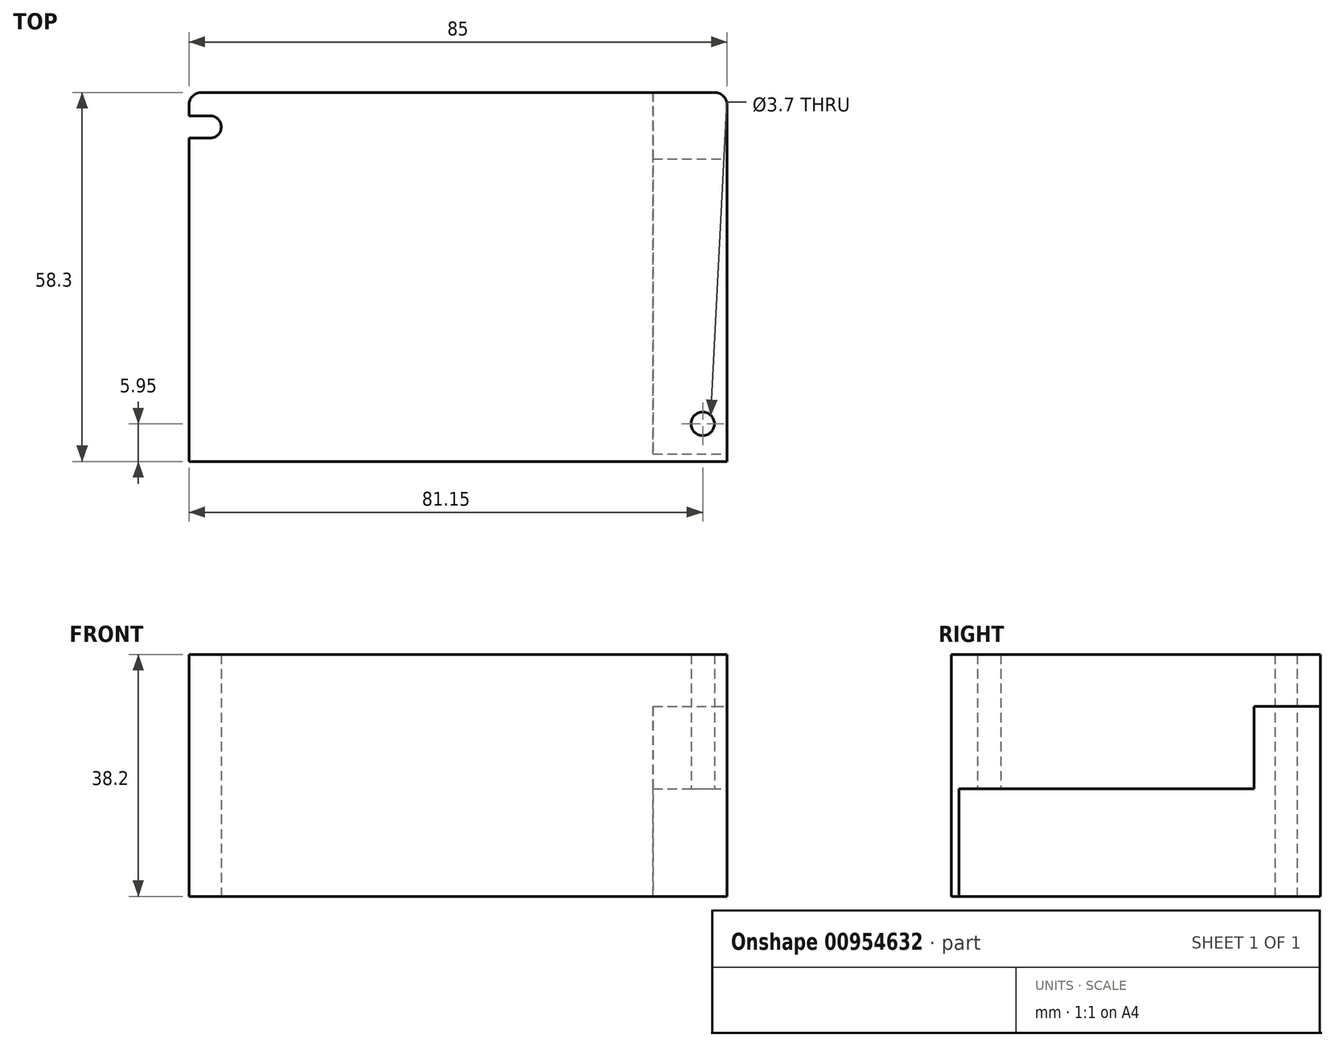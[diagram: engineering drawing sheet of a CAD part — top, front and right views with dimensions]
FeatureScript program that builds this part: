
annotation { "Feature Type Name" : "Feature", "Feature Type Description" : "" }
export const myFeature = defineFeature(function(context is Context, id is Id, definition is map)
    precondition{}
    {
        {
            var Q0;
            Q0=qCreatedBy(makeId("Top.planeOp"),FACE);
            var sketch = newSketch(context, id + "F0", { "sketchPlane" : qUnion([Q0])});
            skLineSegment(sketch, "E0.bottom", {"start": v(40.5, 29.15) * mm, "end": v(-40.5, 29.15) * mm});
            skLineSegment(sketch, "E0.top", {"start": v(42.5, -29.15) * mm, "end": v(-42.5, -29.15) * mm});
            skLineSegment(sketch, "E0.left", {"start": v(42.5, 27.15) * mm, "end": v(42.5, -29.15) * mm});
            skLineSegment(sketch, "E0.right", {"start": v(-42.5, 27.15) * mm, "end": v(-42.5, -29.15) * mm});
            skPoint(sketch, "E0.middle", {"position": v(0, 0) * mm});
            skPoint(sketch, "E1.visualSharp", {"position": v(-42.5, 29.15) * mm});
            skArc(sketch, "E1.filletArc", {"start": v(-40.5, 29.15) * mm, "mid": v(-41.91, 28.56) * mm, "end": v(-42.5, 27.15) * mm});
            skPoint(sketch, "E2.visualSharp", {"position": v(42.5, 29.15) * mm});
            skArc(sketch, "E2.filletArc", {"start": v(42.5, 27.15) * mm, "mid": v(41.91, 28.56) * mm, "end": v(40.5, 29.15) * mm});
            skLineSegment(sketch, "E3", {"start": v(-42.5, 25.45) * mm, "end": v(-39.15, 25.45) * mm});
            skLineSegment(sketch, "E4", {"start": v(-42.5, 21.95) * mm, "end": v(-39.15, 21.95) * mm});
            skArc(sketch, "E5", {"start": v(-39.15, 25.45) * mm, "mid": v(-37.4, 23.7) * mm, "end": v(-39.15, 21.95) * mm});
            skCircle(sketch, "E6", {"center": v(38.65, -23.2) * mm, "radius": 1.85 * mm});
            skSolve(sketch);
        }
        {
            var Q0;
            Q0=makeQuery(id+"F0.imprint","IMPRINT",FACE,{"disambiguationData":[TD([[makeQuery(id+"F0.imprint","IMPRINT",EDGE,{"derivedFrom":sQuery(id+"F0.wireOp",EDGE,"E0.bottom")}),1.0]])]});
            extrude(context, id + "F1", {"entities" : qUnion([Q0]), "depth" : 38.2 * mm, "offsetDistance" : 25 * mm});
        }
        {
            var Q0;
            Q0=makeQuery(id+"F1.opExtrude","SWEPT_FACE",FACE,{"disambiguationData":[OSD([sQuery(id+"F0.wireOp",EDGE,"E0.left")])]});
            var sketch = newSketch(context, id + "F2", { "sketchPlane" : qUnion([Q0])});
            skLineSegment(sketch, "E7.0.0", {"start": v(-29.15, 0) * mm, "end": v(27.15, 0) * mm});
            skLineSegment(sketch, "E7.0.1", {"start": v(27.15, 0) * mm, "end": v(27.15, 38.2) * mm});
            skLineSegment(sketch, "E7.0.2", {"start": v(27.15, 38.2) * mm, "end": v(-29.15, 38.2) * mm});
            skLineSegment(sketch, "E7.0.3", {"start": v(-29.15, 38.2) * mm, "end": v(-29.15, 0) * mm});
            skLineSegment(sketch, "E8", {"start": v(-27.95, 0) * mm, "end": v(-27.95, 17) * mm});
            skLineSegment(sketch, "E9", {"start": v(-27.95, 17) * mm, "end": v(18.65, 17) * mm});
            skLineSegment(sketch, "E10", {"start": v(18.65, 17) * mm, "end": v(18.65, 30) * mm});
            skLineSegment(sketch, "E11", {"start": v(18.65, 30) * mm, "end": v(29.15, 30) * mm});
            skLineSegment(sketch, "E12", {"start": v(29.15, 30) * mm, "end": v(29.15, 0) * mm});
            skLineSegment(sketch, "E13", {"start": v(29.15, 0) * mm, "end": v(27.15, 0) * mm});
            skLineSegment(sketch, "E14.0", {"start": v(29.15, 38.2) * mm, "end": v(29.15, 0) * mm, "construction": true});
            skSolve(sketch);
        }
        {
            var Q0;
            {var subQ0=sQuery(id+"F2.wireOp",EDGE,"E8");Q0=makeQuery(id+"F2.imprint","IMPRINT",FACE,{"disambiguationData":[TD([[makeQuery(id+"F2.imprint","IMPRINT",EDGE,{"derivedFrom":subQ0}),-1.0]])]});}
            var Q1;
            {var subQ4=sQuery(id+"F2.wireOp",EDGE,"E12");Q1=makeQuery(id+"F2.imprint","IMPRINT",FACE,{"disambiguationData":[TD([[makeQuery(id+"F2.imprint","IMPRINT",EDGE,{"derivedFrom":subQ4}),-1.0]])]});}
            extrude(context, id + "F3", {"entities" : qUnion([Q0, Q1]), "operationType" : NewBodyOperationType.REMOVE, "oppositeDirection" : true, "depth" : 11.7 * mm, "offsetDistance" : 25 * mm});
        }
    });
